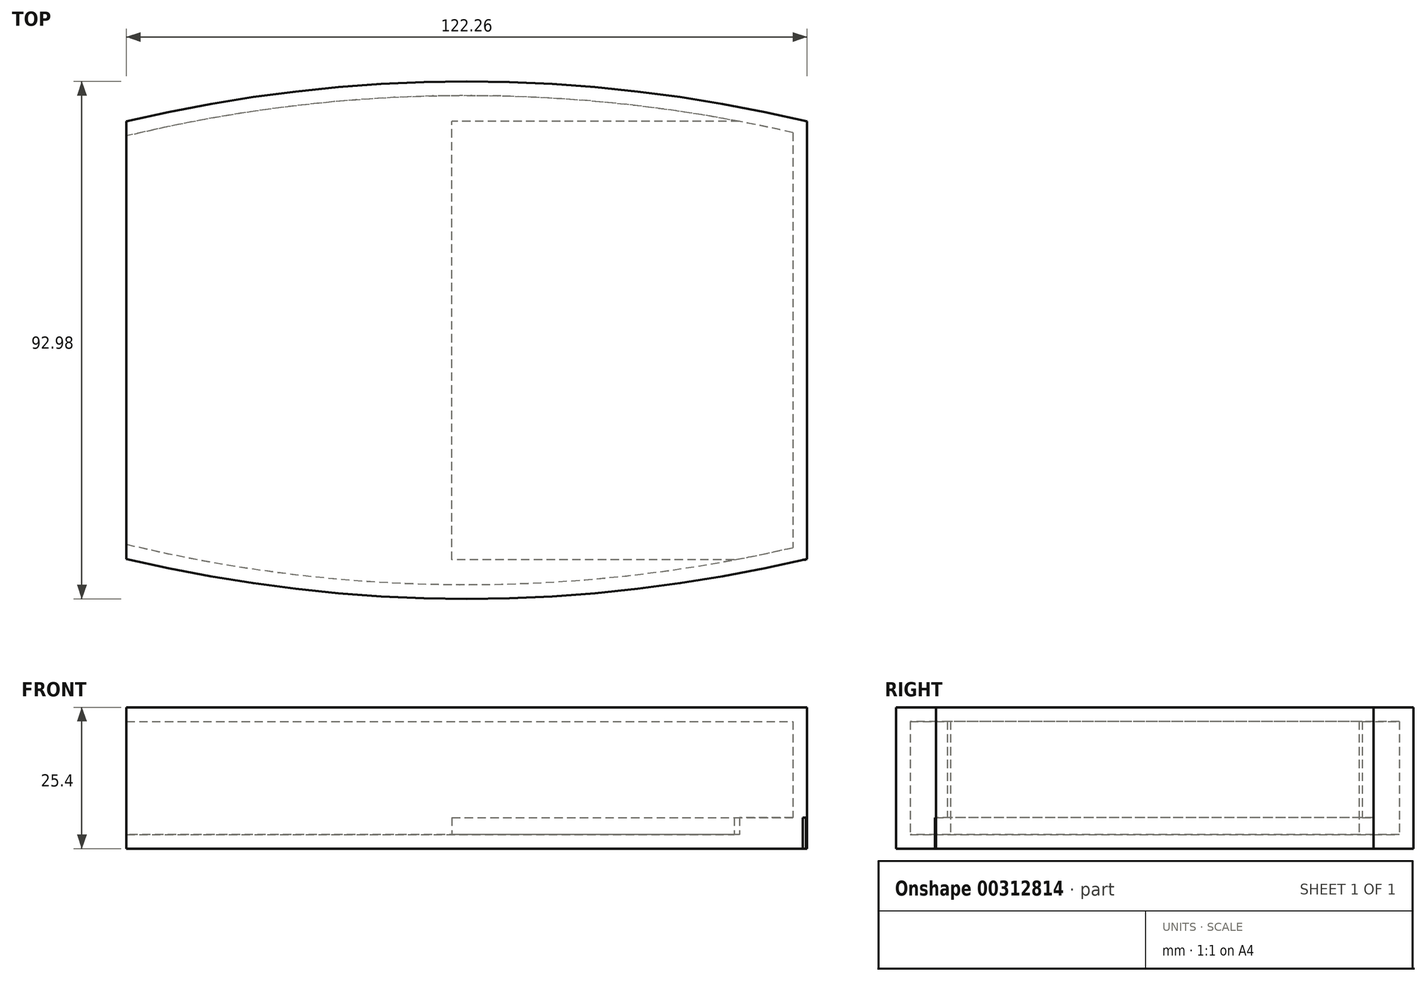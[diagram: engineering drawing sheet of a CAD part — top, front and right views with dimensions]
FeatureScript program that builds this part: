
annotation { "Feature Type Name" : "Feature", "Feature Type Description" : "" }
export const myFeature = defineFeature(function(context is Context, id is Id, definition is map)
    precondition{}
    {
        {
            var Q0;
            Q0=qCreatedBy(makeId("Top.planeOp"),FACE);
            var sketch = newSketch(context, id + "F0", { "sketchPlane" : qUnion([Q0])});
            skLineSegment(sketch, "E0.bottom", {"start": v(-58.47, 35.65) * mm, "end": v(63.79, 35.65) * mm});
            skLineSegment(sketch, "E0.top", {"start": v(-58.47, -42.98) * mm, "end": v(63.79, -42.98) * mm});
            skLineSegment(sketch, "E0.left", {"start": v(-58.47, 35.65) * mm, "end": v(-58.47, -42.98) * mm});
            skLineSegment(sketch, "E0.right", {"start": v(63.79, 35.65) * mm, "end": v(63.79, -42.98) * mm});
            skArc(sketch, "E1", {"start": v(63.79, 35.65) * mm, "mid": v(2.66, 42.82) * mm, "end": v(-58.47, 35.65) * mm});
            skArc(sketch, "E2", {"start": v(-58.47, -42.98) * mm, "mid": v(2.66, -50.16) * mm, "end": v(63.79, -42.98) * mm});
            skSolve(sketch);
        }
        {
            var Q0;
            Q0=qCreatedBy(makeId("Top.planeOp"),FACE);
            var sketch = newSketch(context, id + "F1", { "sketchPlane" : qUnion([Q0])});
            skLineSegment(sketch, "E3.bottom", {"start": v(0, 35.65) * mm, "end": v(63.6, 35.65) * mm});
            skLineSegment(sketch, "E3.top", {"start": v(0, -43.17) * mm, "end": v(63.6, -43.17) * mm});
            skLineSegment(sketch, "E3.left", {"start": v(0, 35.65) * mm, "end": v(0, -43.17) * mm});
            skLineSegment(sketch, "E3.right", {"start": v(63.6, 35.65) * mm, "end": v(63.6, -43.17) * mm});
            skSolve(sketch);
        }
        {
            var Q0;
            Q0 = qSketchRegion(id + "F0", true);
            extrude(context, id + "F2", {"entities" : qUnion([Q0]), "depth" : 25.4 * mm});
        }
        {
            var Q0;
            Q0=makeQuery(id+"F2.opExtrude","SWEPT_FACE",FACE,{"disambiguationData":[OSD([sQuery(id+"F0.wireOp",EDGE,"E0.left")])]});
            shell(context, id + "F3", {"entities" : qUnion([Q0]), "thickness" : 2.54 * mm});
        }
        {
            var Q0;
            Q0 = qSketchRegion(id + "F1", true);
            extrude(context, id + "F4", {"entities" : qUnion([Q0]), "operationType" : NewBodyOperationType.ADD, "depth" : 5.6 * mm});
        }
        {
            var Q0;
            Q0=qCreatedBy(makeId("Front.planeOp"),FACE);
            var sketch = newSketch(context, id + "F5", { "sketchPlane" : qUnion([Q0])});
            skCircle(sketch, "E4", {"center": v(-13.2, 4.86) * mm, "radius": 1.64 * mm});
            skCircle(sketch, "E5", {"center": v(-47.84, 4.86) * mm, "radius": 1.64 * mm});
            skSolve(sketch);
        }
        {
            var Q0;
            Q0=makeQuery(id+"F5.imprint","IMPRINT",FACE,{"disambiguationData":[TD([[makeQuery(id+"F5.imprint","IMPRINT",EDGE,{"derivedFrom":sQuery(id+"F5.wireOp",EDGE,"E5")}),1.0]])]});
            extrude(context, id + "F6", {"entities" : qUnion([Q0]), "operationType" : NewBodyOperationType.REMOVE, "oppositeDirection" : true, "depth" : 28.2 * mm});
        }
        {
            var Q0;
            Q0 = qSketchRegion(id + "F5", true);
            extrude(context, id + "F7", {"entities" : qUnion([Q0]), "operationType" : NewBodyOperationType.REMOVE, "oppositeDirection" : true, "depth" : 32.26 * mm});
        }
        {
            var Q0;
            Q0=sQuery(id+"F0.wireOp",EDGE,"E0.bottom");
            var Q1;
            Q1=sQuery(id+"F0.wireOp",EDGE,"E1");
            extrude(context, id + "F8", {"bodyType" : ToolBodyType.SURFACE, "surfaceEntities" : qUnion([Q0, Q1]), "depth" : 25.4 * mm});
        }
        {
            var Q0;
            Q0=sQuery(id+"F0.wireOp",EDGE,"E0.top");
            var Q1;
            Q1=sQuery(id+"F0.wireOp",EDGE,"E2");
            extrude(context, id + "F9", {"bodyType" : ToolBodyType.SURFACE, "surfaceEntities" : qUnion([Q0, Q1]), "depth" : 25.4 * mm});
        }
    });
